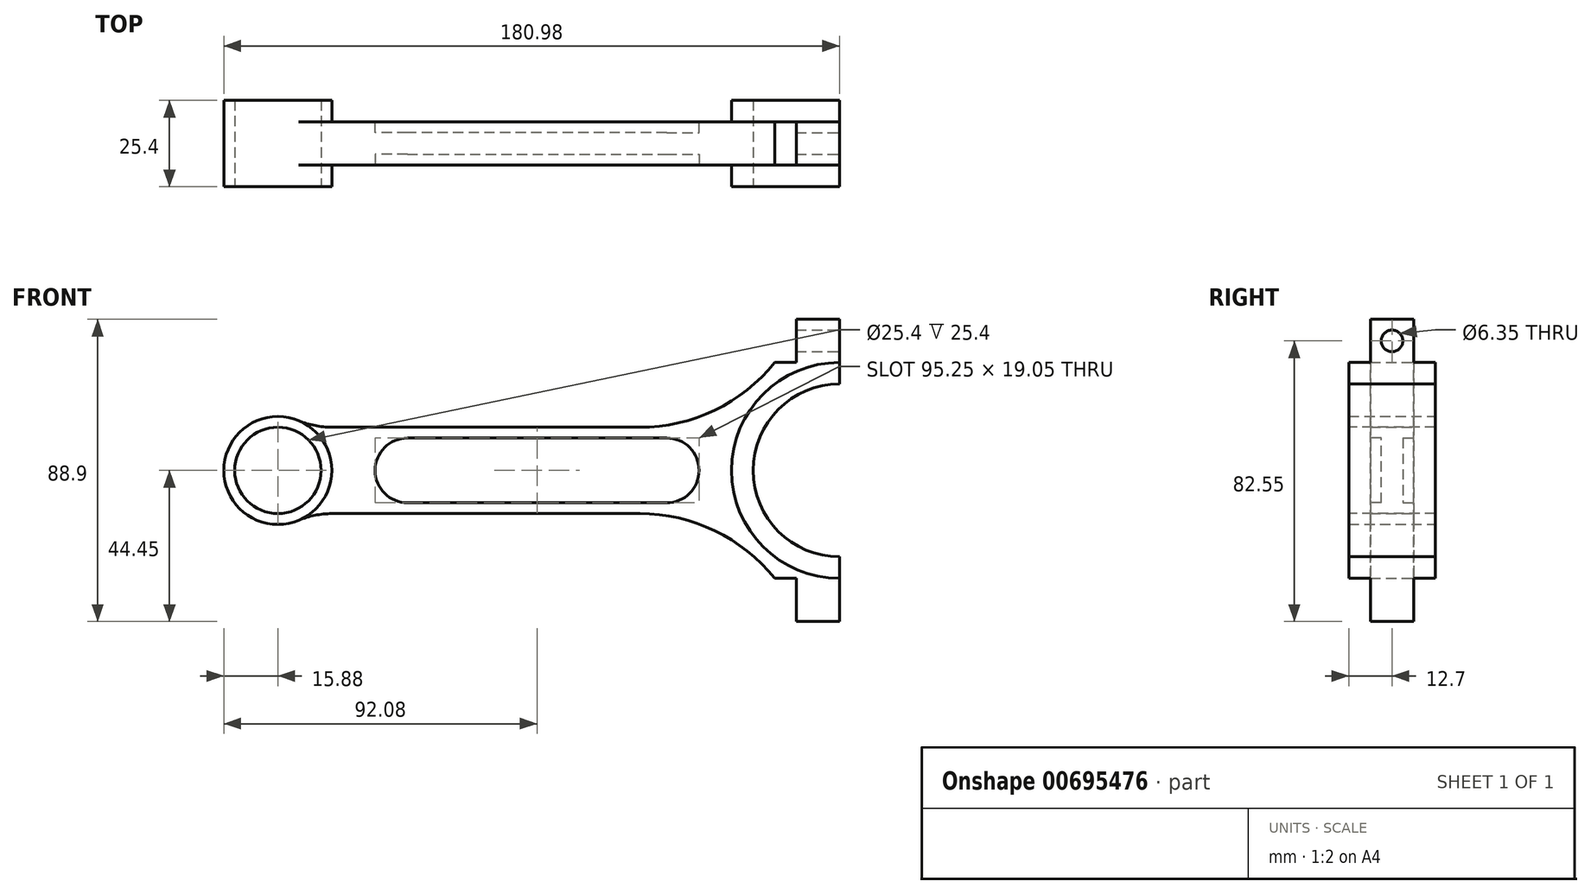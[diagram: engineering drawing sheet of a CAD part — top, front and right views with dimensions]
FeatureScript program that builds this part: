
annotation { "Feature Type Name" : "Feature", "Feature Type Description" : "" }
export const myFeature = defineFeature(function(context is Context, id is Id, definition is map)
    precondition{}
    {
        {
            var Q0;
            Q0=qCreatedBy(makeId("Front.planeOp"),FACE);
            var sketch = newSketch(context, id + "F0", { "sketchPlane" : qUnion([Q0])});
            skArc(sketch, "E0", {"start": v(0, 25.4) * mm, "mid": v(-25.4, 0) * mm, "end": v(0, -25.4) * mm});
            skArc(sketch, "E1", {"start": v(-159, 14.65) * mm, "mid": v(-180.98, 0) * mm, "end": v(-159, -14.65) * mm});
            skArc(sketch, "E2", {"start": v(-159, 14.65) * mm, "mid": v(-154.2, 13.2) * mm, "end": v(-149.23, 12.7) * mm});
            skLineSegment(sketch, "E3.trimOffspring", {"start": v(-149.23, 12.7) * mm, "end": v(-58.7, 12.7) * mm});
            skLineSegment(sketch, "E4.bottom", {"start": v(0, -44.45) * mm, "end": v(-12.7, -44.45) * mm});
            skLineSegment(sketch, "E4.top", {"start": v(0, 44.45) * mm, "end": v(-12.7, 44.45) * mm});
            skLineSegment(sketch, "E4.left", {"start": v(0, -44.45) * mm, "end": v(0, -25.4) * mm});
            skLineSegment(sketch, "E4.right", {"start": v(-12.7, -44.45) * mm, "end": v(-12.7, -31.75) * mm});
            skPoint(sketch, "E5", {"position": v(-12.7, 31.75) * mm});
            skLineSegment(sketch, "E6", {"start": v(-12.7, 31.75) * mm, "end": v(-19.05, 31.75) * mm});
            skArc(sketch, "E7.trimOffspring", {"start": v(-58.7, 12.7) * mm, "mid": v(-36.7, 17.7) * mm, "end": v(-19.05, 31.75) * mm});
            skPoint(sketch, "E8", {"position": v(-12.7, -31.75) * mm});
            skLineSegment(sketch, "E9", {"start": v(-12.7, -31.75) * mm, "end": v(-19.05, -31.75) * mm});
            skArc(sketch, "E10.trimOffspring", {"start": v(-19.05, -31.75) * mm, "mid": v(-36.7, -17.7) * mm, "end": v(-58.7, -12.7) * mm});
            skLineSegment(sketch, "E11.trimOffspring", {"start": v(-12.7, 31.75) * mm, "end": v(-12.7, 44.45) * mm});
            skArc(sketch, "E12", {"start": v(-149.23, -12.7) * mm, "mid": v(-154.2, -13.2) * mm, "end": v(-159, -14.65) * mm});
            skLineSegment(sketch, "E13.trimOffspring", {"start": v(-149.23, -12.7) * mm, "end": v(-58.7, -12.7) * mm});
            skLineSegment(sketch, "E14.trimOffspring", {"start": v(0, 25.4) * mm, "end": v(0, 44.45) * mm});
            skSolve(sketch);
        }
        {
            var Q0;
            Q0=makeQuery(id+"F0.imprint","IMPRINT",FACE,{"disambiguationData":[TD([[makeQuery(id+"F0.imprint","IMPRINT",EDGE,{"derivedFrom":sQuery(id+"F0.wireOp",EDGE,"E0")}),-1.0]])]});
            extrude(context, id + "F1", {"entities" : qUnion([Q0]), "depth" : 12.7 * mm, "offsetDistance" : 25.4 * mm, "symmetric" : true});
        }
        {
            var Q0;
            Q0=makeQuery(id+"F1.opExtrude","CAP_FACE",FACE,{"disambiguationData":[OSD([sQuery(id+"F0.wireOp",EDGE,"E0"),sQuery(id+"F0.wireOp",EDGE,"E1"),sQuery(id+"F0.wireOp",EDGE,"E2"),sQuery(id+"F0.wireOp",EDGE,"E3.trimOffspring"),sQuery(id+"F0.wireOp",EDGE,"E4.bottom"),sQuery(id+"F0.wireOp",EDGE,"E4.top"),sQuery(id+"F0.wireOp",EDGE,"E4.left"),sQuery(id+"F0.wireOp",EDGE,"E4.right"),sQuery(id+"F0.wireOp",EDGE,"E6"),sQuery(id+"F0.wireOp",EDGE,"E7.trimOffspring"),sQuery(id+"F0.wireOp",EDGE,"E9"),sQuery(id+"F0.wireOp",EDGE,"E10.trimOffspring"),sQuery(id+"F0.wireOp",EDGE,"E11.trimOffspring"),sQuery(id+"F0.wireOp",EDGE,"E12"),sQuery(id+"F0.wireOp",EDGE,"E13.trimOffspring"),sQuery(id+"F0.wireOp",EDGE,"E14.trimOffspring")])],"isStart":false});
            var sketch = newSketch(context, id + "F2", { "sketchPlane" : qUnion([Q0])});
            skLineSegment(sketch, "E15.bottom", {"start": v(-127, -9.53) * mm, "end": v(-50.8, -9.53) * mm});
            skLineSegment(sketch, "E15.top", {"start": v(-127, 9.53) * mm, "end": v(-50.8, 9.53) * mm});
            skArc(sketch, "E16", {"start": v(-50.8, -9.53) * mm, "mid": v(-41.28, 0) * mm, "end": v(-50.8, 9.53) * mm});
            skArc(sketch, "E17", {"start": v(-127, 9.53) * mm, "mid": v(-136.53, 0) * mm, "end": v(-127, -9.52) * mm});
            skSolve(sketch);
        }
        {
            var Q0;
            Q0 = qSketchRegion(id + "F2", true);
            extrude(context, id + "F3", {"entities" : qUnion([Q0]), "operationType" : NewBodyOperationType.REMOVE, "oppositeDirection" : true, "depth" : 3.17 * mm, "offsetDistance" : 25.4 * mm});
        }
        {
            var Q0;
            Q0=makeQuery(id+"F1.opExtrude","CAP_FACE",FACE,{"disambiguationData":[OSD([sQuery(id+"F0.wireOp",EDGE,"E0"),sQuery(id+"F0.wireOp",EDGE,"E1"),sQuery(id+"F0.wireOp",EDGE,"E2"),sQuery(id+"F0.wireOp",EDGE,"E3.trimOffspring"),sQuery(id+"F0.wireOp",EDGE,"E4.bottom"),sQuery(id+"F0.wireOp",EDGE,"E4.top"),sQuery(id+"F0.wireOp",EDGE,"E4.left"),sQuery(id+"F0.wireOp",EDGE,"E4.right"),sQuery(id+"F0.wireOp",EDGE,"E6"),sQuery(id+"F0.wireOp",EDGE,"E7.trimOffspring"),sQuery(id+"F0.wireOp",EDGE,"E9"),sQuery(id+"F0.wireOp",EDGE,"E10.trimOffspring"),sQuery(id+"F0.wireOp",EDGE,"E11.trimOffspring"),sQuery(id+"F0.wireOp",EDGE,"E12"),sQuery(id+"F0.wireOp",EDGE,"E13.trimOffspring"),sQuery(id+"F0.wireOp",EDGE,"E14.trimOffspring")])],"isStart":true});
            var sketch = newSketch(context, id + "F4", { "sketchPlane" : qUnion([Q0])});
            skLineSegment(sketch, "E18.bottom", {"start": v(50.8, -9.53) * mm, "end": v(127, -9.53) * mm});
            skLineSegment(sketch, "E18.top", {"start": v(50.8, 9.53) * mm, "end": v(127, 9.53) * mm});
            skArc(sketch, "E19", {"start": v(50.8, 9.53) * mm, "mid": v(41.28, 0) * mm, "end": v(50.8, -9.53) * mm});
            skArc(sketch, "E20", {"start": v(127, -9.52) * mm, "mid": v(136.53, 0) * mm, "end": v(127, 9.52) * mm});
            skSolve(sketch);
        }
        {
            var Q0;
            Q0=makeQuery(id+"F4.imprint","IMPRINT",FACE,{"disambiguationData":[TD([[makeQuery(id+"F4.imprint","IMPRINT",EDGE,{"derivedFrom":sQuery(id+"F4.wireOp",EDGE,"E18.bottom")}),1.0]])]});
            extrude(context, id + "F5", {"entities" : qUnion([Q0]), "operationType" : NewBodyOperationType.REMOVE, "oppositeDirection" : true, "depth" : 3.17 * mm, "offsetDistance" : 25.4 * mm});
        }
        {
            var Q0;
            Q0=qCreatedBy(makeId("Front.planeOp"),FACE);
            var sketch = newSketch(context, id + "F6", { "sketchPlane" : qUnion([Q0])});
            skPoint(sketch, "E21", {"position": v(-165.1, 0) * mm});
            skCircle(sketch, "E22", {"center": v(-165.1, 0) * mm, "radius": 15.88 * mm});
            skSolve(sketch);
        }
        {
            var Q0;
            Q0 = qSketchRegion(id + "F6", true);
            extrude(context, id + "F7", {"entities" : qUnion([Q0]), "operationType" : NewBodyOperationType.ADD, "depth" : 25.4 * mm, "offsetDistance" : 25.4 * mm, "symmetric" : true});
        }
        {
            var Q0;
            Q0=qCreatedBy(makeId("Front.planeOp"),FACE);
            var sketch = newSketch(context, id + "F8", { "sketchPlane" : qUnion([Q0])});
            skArc(sketch, "E23", {"start": v(0, 31.75) * mm, "mid": v(-31.75, 0) * mm, "end": v(0, -31.75) * mm});
            skLineSegment(sketch, "E24", {"start": v(0, 31.75) * mm, "end": v(0, -31.75) * mm});
            skSolve(sketch);
        }
        {
            var Q0;
            Q0 = qSketchRegion(id + "F8", true);
            extrude(context, id + "F9", {"entities" : qUnion([Q0]), "operationType" : NewBodyOperationType.ADD, "depth" : 25.4 * mm, "offsetDistance" : 25.4 * mm, "symmetric" : true});
        }
        {
            var Q0;
            Q0=makeQuery(id+"F9.opExtrude","CAP_FACE",FACE,{"disambiguationData":[OSD([sQuery(id+"F8.wireOp",EDGE,"E23"),sQuery(id+"F8.wireOp",EDGE,"E24")])],"isStart":false});
            var sketch = newSketch(context, id + "F10", { "sketchPlane" : qUnion([Q0])});
            skArc(sketch, "E25", {"start": v(0, 25.4) * mm, "mid": v(-25.4, 0) * mm, "end": v(0, -25.4) * mm});
            skLineSegment(sketch, "E26", {"start": v(0, 25.4) * mm, "end": v(0, -25.4) * mm});
            skSolve(sketch);
        }
        {
            var Q0;
            Q0=makeQuery(id+"F10.imprint","IMPRINT",FACE,{"disambiguationData":[TD([[makeQuery(id+"F10.imprint","IMPRINT",EDGE,{"derivedFrom":sQuery(id+"F10.wireOp",EDGE,"E25")}),1.0]])]});
            extrude(context, id + "F11", {"entities" : qUnion([Q0]), "operationType" : NewBodyOperationType.REMOVE, "endBound" : BoundingType.THROUGH_ALL, "oppositeDirection" : true, "depth" : 25.4 * mm, "offsetDistance" : 25.4 * mm});
        }
        {
            var Q0;
            Q0=makeQuery(id+"F7.opExtrude","CAP_FACE",FACE,{"disambiguationData":[OSD([sQuery(id+"F6.wireOp",EDGE,"E22")])],"isStart":false});
            var sketch = newSketch(context, id + "F12", { "sketchPlane" : qUnion([Q0])});
            skCircle(sketch, "E27", {"center": v(-165.1, 0) * mm, "radius": 12.7 * mm});
            skSolve(sketch);
        }
        {
            var Q0;
            Q0=makeQuery(id+"F12.imprint","IMPRINT",FACE,{"disambiguationData":[TD([[makeQuery(id+"F12.imprint","IMPRINT",EDGE,{"derivedFrom":sQuery(id+"F12.wireOp",EDGE,"E27")}),1.0]])]});
            extrude(context, id + "F13", {"entities" : qUnion([Q0]), "operationType" : NewBodyOperationType.REMOVE, "endBound" : BoundingType.THROUGH_ALL, "oppositeDirection" : true, "depth" : 25.4 * mm, "offsetDistance" : 25.4 * mm});
        }
        {
            var Q0;
            Q0=qCreatedBy(makeId("Right.planeOp"),FACE);
            var sketch = newSketch(context, id + "F14", { "sketchPlane" : qUnion([Q0])});
            skCircle(sketch, "E28", {"center": v(0, 38.1) * mm, "radius": 3.18 * mm});
            skCircle(sketch, "E29.MirrorC", {"center": v(0, -38.1) * mm, "radius": 3.18 * mm});
            skSolve(sketch);
        }
        {
            var Q0;
            Q0=makeQuery(id+"F14.imprint","IMPRINT",FACE,{"disambiguationData":[TD([[makeQuery(id+"F14.imprint","IMPRINT",EDGE,{"derivedFrom":sQuery(id+"F14.wireOp",EDGE,"E28")}),1.0]])]});
            var Q1;
            Q1=makeQuery(id+"F14.imprint","IMPRINT",FACE,{"disambiguationData":[TD([[makeQuery(id+"F14.imprint","IMPRINT",EDGE,{"derivedFrom":sQuery(id+"F14.wireOp",EDGE,"E29.MirrorC")}),-1.0]])]});
            extrude(context, id + "F15", {"entities" : qUnion([Q0, Q1]), "operationType" : NewBodyOperationType.REMOVE, "endBound" : BoundingType.THROUGH_ALL, "oppositeDirection" : true, "depth" : 25.4 * mm, "offsetDistance" : 25.4 * mm});
        }
    });
